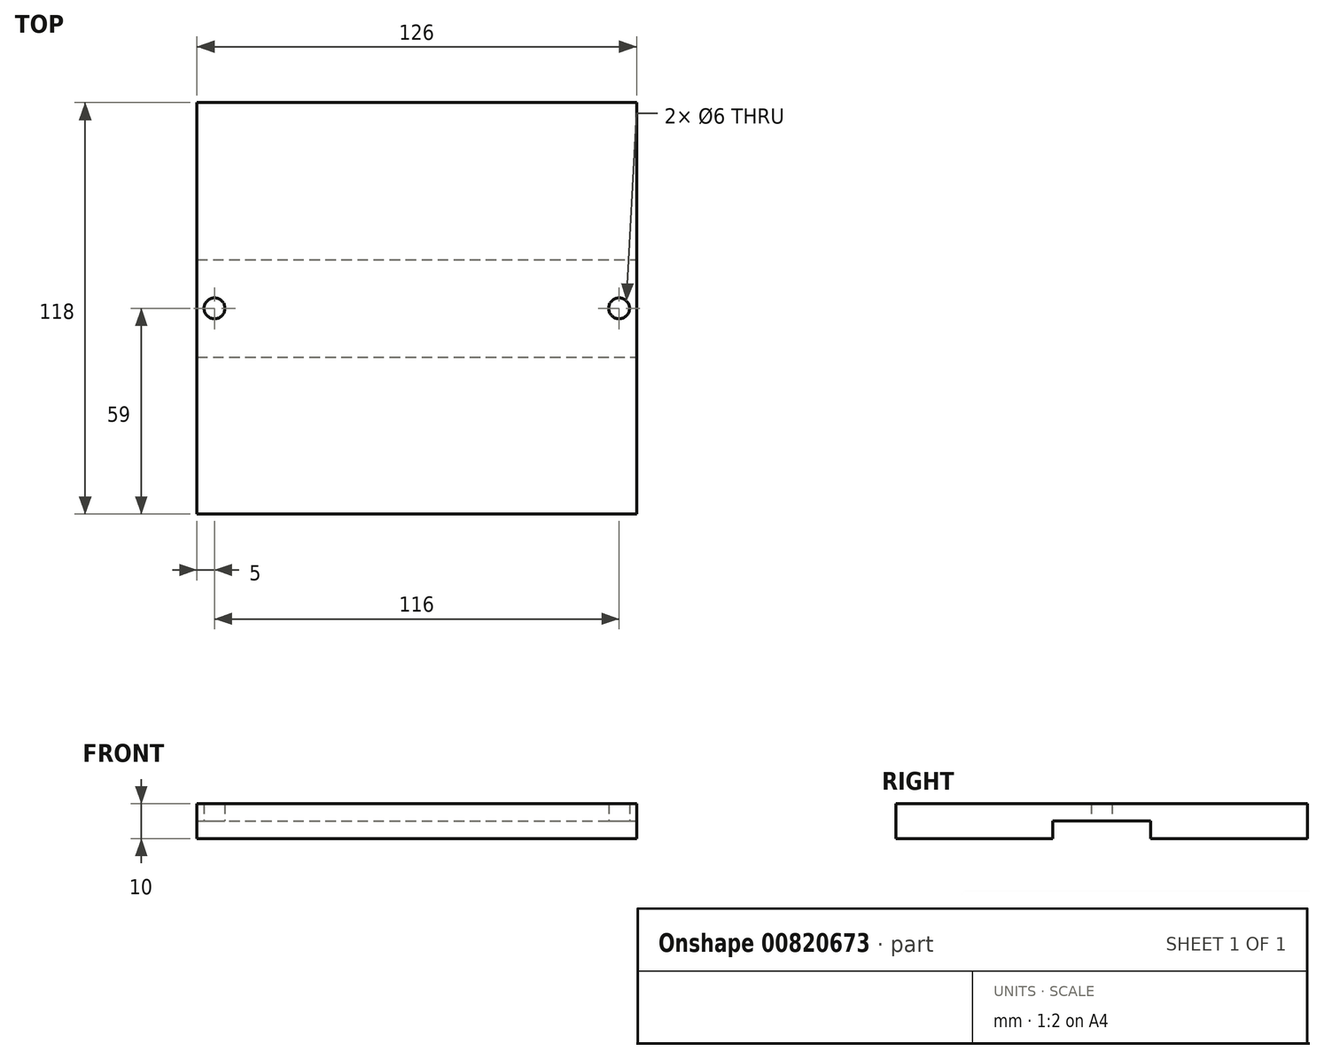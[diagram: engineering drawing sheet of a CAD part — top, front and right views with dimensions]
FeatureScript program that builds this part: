
annotation { "Feature Type Name" : "Feature", "Feature Type Description" : "" }
export const myFeature = defineFeature(function(context is Context, id is Id, definition is map)
    precondition{}
    {
        {
            var Q0;
            Q0=qCreatedBy(makeId("Top.planeOp"),FACE);
            var sketch = newSketch(context, id + "F0", { "sketchPlane" : qUnion([Q0])});
            skLineSegment(sketch, "E0.bottom", {"start": v(-63, 59) * mm, "end": v(63, 59) * mm});
            skLineSegment(sketch, "E0.top", {"start": v(-63, -59) * mm, "end": v(63, -59) * mm});
            skLineSegment(sketch, "E0.left", {"start": v(-63, 59) * mm, "end": v(-63, -59) * mm});
            skLineSegment(sketch, "E0.right", {"start": v(63, 59) * mm, "end": v(63, -59) * mm});
            skCircle(sketch, "E1", {"center": v(-58, 0) * mm, "radius": 3 * mm});
            skCircle(sketch, "E2.MirrorC", {"center": v(58, 0) * mm, "radius": 3 * mm});
            skSolve(sketch);
        }
        {
            var Q0;
            Q0 = qSketchRegion(id + "F0", true);
            extrude(context, id + "F1", {"entities" : qUnion([Q0]), "depth" : 10 * mm, "offsetDistance" : 25 * mm});
        }
        {
            var Q0;
            Q0=makeQuery(id+"F1.opExtrude","SWEPT_FACE",FACE,{"disambiguationData":[OSD([sQuery(id+"F0.wireOp",EDGE,"E0.right")])]});
            var sketch = newSketch(context, id + "F2", { "sketchPlane" : qUnion([Q0])});
            skLineSegment(sketch, "E3", {"start": v(-14, 0) * mm, "end": v(-14, 5) * mm});
            skLineSegment(sketch, "E4", {"start": v(-14, 5) * mm, "end": v(14, 5) * mm});
            skLineSegment(sketch, "E5", {"start": v(14, 5) * mm, "end": v(14, 0) * mm});
            skLineSegment(sketch, "E6", {"start": v(-14, 0) * mm, "end": v(14, 0) * mm});
            skSolve(sketch);
        }
        {
            var Q0;
            Q0=makeQuery(id+"F2.imprint","IMPRINT",FACE,{"disambiguationData":[TD([[makeQuery(id+"F2.imprint","IMPRINT",EDGE,{"derivedFrom":sQuery(id+"F2.wireOp",EDGE,"E3")}),-1.0]])]});
            extrude(context, id + "F3", {"entities" : qUnion([Q0]), "operationType" : NewBodyOperationType.REMOVE, "endBound" : BoundingType.THROUGH_ALL, "oppositeDirection" : true, "depth" : -25 * mm, "offsetDistance" : 25 * mm});
        }
    });
